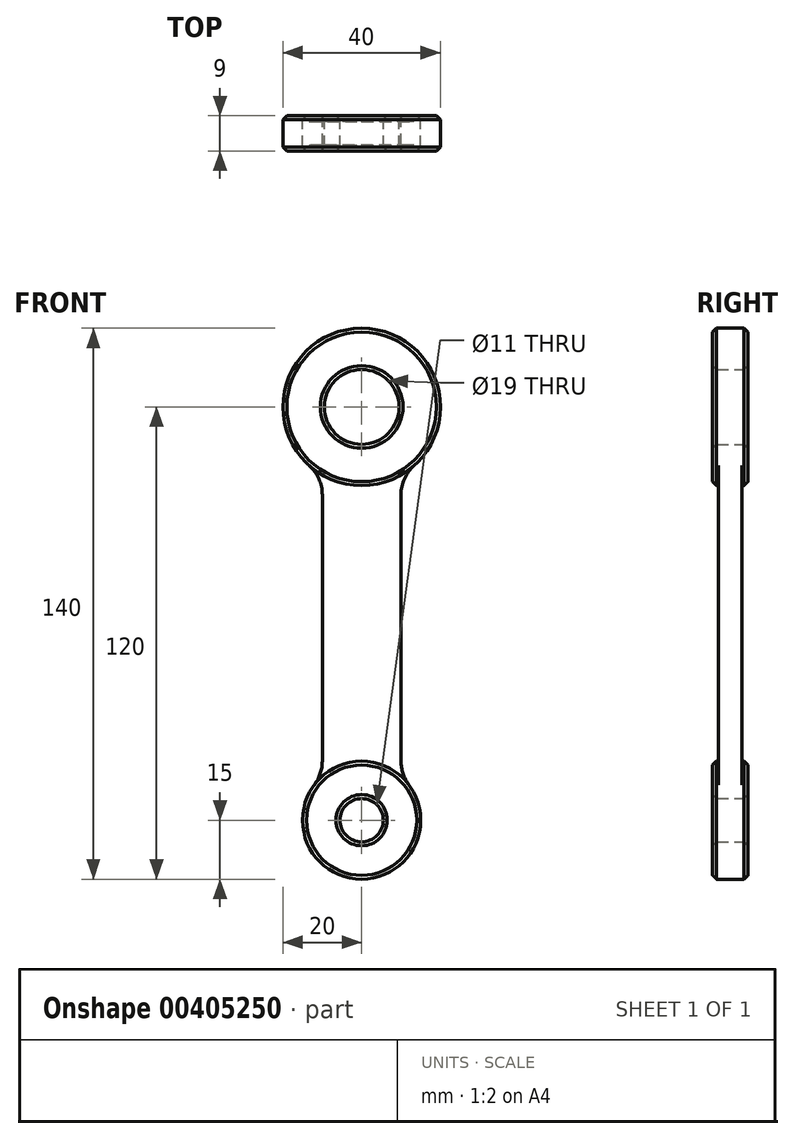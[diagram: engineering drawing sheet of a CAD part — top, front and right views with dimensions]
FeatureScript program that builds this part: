
annotation { "Feature Type Name" : "Feature", "Feature Type Description" : "" }
export const myFeature = defineFeature(function(context is Context, id is Id, definition is map)
    precondition{}
    {
        {
            var Q0;
            Q0=qCreatedBy(makeId("Front.planeOp"),FACE);
            var sketch = newSketch(context, id + "F0", { "sketchPlane" : qUnion([Q0])});
            skCircle(sketch, "E0", {"center": v(0, 0) * mm, "radius": 5.5 * mm});
            skCircle(sketch, "E1", {"center": v(0, 105) * mm, "radius": 9.5 * mm});
            skCircle(sketch, "E2", {"center": v(0, 105) * mm, "radius": 20 * mm});
            skCircle(sketch, "E3", {"center": v(0, 0) * mm, "radius": 15 * mm});
            skLineSegment(sketch, "E4", {"start": v(-10, 82.64) * mm, "end": v(-10, 15) * mm});
            skLineSegment(sketch, "E5", {"start": v(10, 82.64) * mm, "end": v(10, 15) * mm});
            skArc(sketch, "E6", {"start": v(-10, 82.64) * mm, "mid": v(-10.87, 86.72) * mm, "end": v(-13.33, 90.1) * mm});
            skArc(sketch, "E7", {"start": v(13.33, 90.1) * mm, "mid": v(10.87, 86.72) * mm, "end": v(10, 82.64) * mm});
            skArc(sketch, "E8", {"start": v(10, 15) * mm, "mid": v(10.51, 11.84) * mm, "end": v(12, 9) * mm});
            skArc(sketch, "E9", {"start": v(-12, 9) * mm, "mid": v(-10.51, 11.84) * mm, "end": v(-10, 15) * mm});
            skSolve(sketch);
        }
        {
            var Q0;
            Q0=makeQuery(id+"F0.imprint","IMPRINT",FACE,{"disambiguationData":[TD([[makeQuery(id+"F0.imprint","IMPRINT",EDGE,{"derivedFrom":sQuery(id+"F0.wireOp",EDGE,"E4")}),1.0]])]});
            extrude(context, id + "F1", {"entities" : qUnion([Q0]), "endBound" : BoundingType.SYMMETRIC, "depth" : 6 * mm});
        }
        {
            var Q0;
            Q0=makeQuery(id+"F0.imprint","IMPRINT",FACE,{"disambiguationData":[TD([[makeQuery(id+"F0.imprint","IMPRINT",EDGE,{"derivedFrom":sQuery(id+"F0.wireOp",EDGE,"E1")}),-1.0]])]});
            var Q1;
            Q1=makeQuery(id+"F0.imprint","IMPRINT",FACE,{"disambiguationData":[TD([[makeQuery(id+"F0.imprint","IMPRINT",EDGE,{"derivedFrom":sQuery(id+"F0.wireOp",EDGE,"E0")}),-1.0]])]});
            extrude(context, id + "F2", {"entities" : qUnion([Q0, Q1]), "operationType" : NewBodyOperationType.ADD, "endBound" : BoundingType.SYMMETRIC, "depth" : 9 * mm});
        }
        {
            var Q0;
            Q0=makeQuery(id+"F2.opExtrude","CAP_FACE",FACE,{"disambiguationData":[OSD([sQuery(id+"F0.wireOp",EDGE,"E1"),sQuery(id+"F0.wireOp",EDGE,"E2")])],"isStart":false});
            var Q1;
            Q1=makeQuery(id+"F2.opExtrude","CAP_FACE",FACE,{"disambiguationData":[OSD([sQuery(id+"F0.wireOp",EDGE,"E0"),sQuery(id+"F0.wireOp",EDGE,"E3")])],"isStart":false});
            var Q2;
            Q2=makeQuery(id+"F2.opExtrude","CAP_EDGE",EDGE,{"disambiguationData":[OSD([sQuery(id+"F0.wireOp",EDGE,"E3")])],"isStart":true});
            var Q3;
            Q3=makeQuery(id+"F2.opExtrude","CAP_EDGE",EDGE,{"disambiguationData":[OSD([sQuery(id+"F0.wireOp",EDGE,"E0")])],"isStart":true});
            var Q4;
            Q4=makeQuery(id+"F2.opExtrude","CAP_FACE",FACE,{"disambiguationData":[OSD([sQuery(id+"F0.wireOp",EDGE,"E1"),sQuery(id+"F0.wireOp",EDGE,"E2")])],"isStart":true});
            chamfer(context, id + "F3", {"entities" : qUnion([Q0, Q1, Q2, Q3, Q4]), "width" : 1 * mm, "tangentPropagation" : true});
        }
    });
